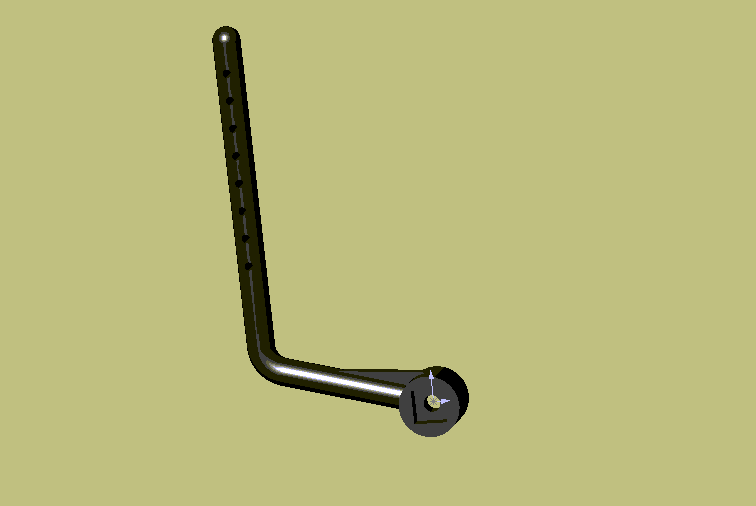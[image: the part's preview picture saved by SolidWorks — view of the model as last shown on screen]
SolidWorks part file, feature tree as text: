
SOLIDWORKS PART (.sldprt)
format: sldprt  version: not decoded by parser v0  size: 234,496 bytes
history: native  units: mm
features: sketch x7, plane x4, extrude x3, cut_extrude x2, material x1, sweep x1, fillet x1 (+8 scaffold rows collapsed)
feature tree (27):
  scaffold x8  (default folders/planes/origin — collapsed)
  material  "Matériau <non spécifié>"
  plane  "Plane1"
  plane  "Plane2"
  plane  "Plane3"
  sketch  "Esquisse1"  dims[D1=11.0mm D2=6.0mm D3=6.0mm D4=3.0mm D5=3.0mm]
  extrude  "Base-Extrusion"  Depth=8mm
  sketch  "Esquisse2"  dims[D1=11.0mm D2=6.0mm D3=6.0mm D4=3.0mm D5=3.0mm]
  extrude  "Boss.-Extru.1"  Depth=3mm
  sketch  "Esquisse3"  dims[D1=3.0mm]
  cut_extrude  "Enlèv. mat.-Extru.1"  [1 undecoded]
  sketch  "Esquisse4"  dims[c1.D3=5.0mm c1.D1=~40.853396mm c2.D1=15.0deg c2.D2=30.0mm c2.D4=70.0mm]
  plane  "Plan1"  Offset=70mm
  sketch  "Esquisse6"  dims[D1=5.0mm]
  sweep  "Boss.-Balayage1"
  fillet  "Congé1"  Radius=2.5mm
  sketch  "Esquisse7"  dims[D3=1.5mm D1=30.0mm D2=27.0mm]
  cut_extrude  "Enlèv. mat.-Extru.2"  Depth=23mm
  sketch  "Esquisse8"
  extrude  "Boss.-Extru.2"  Depth=2mm
decode coverage: 11 of 14 modeling features carry decoded parameters
note: ~ marks probable driven/reference dimensions
note: 1 parameter value undecoded
note: suppression state not decoded; provenance and decode notes live in map.json
